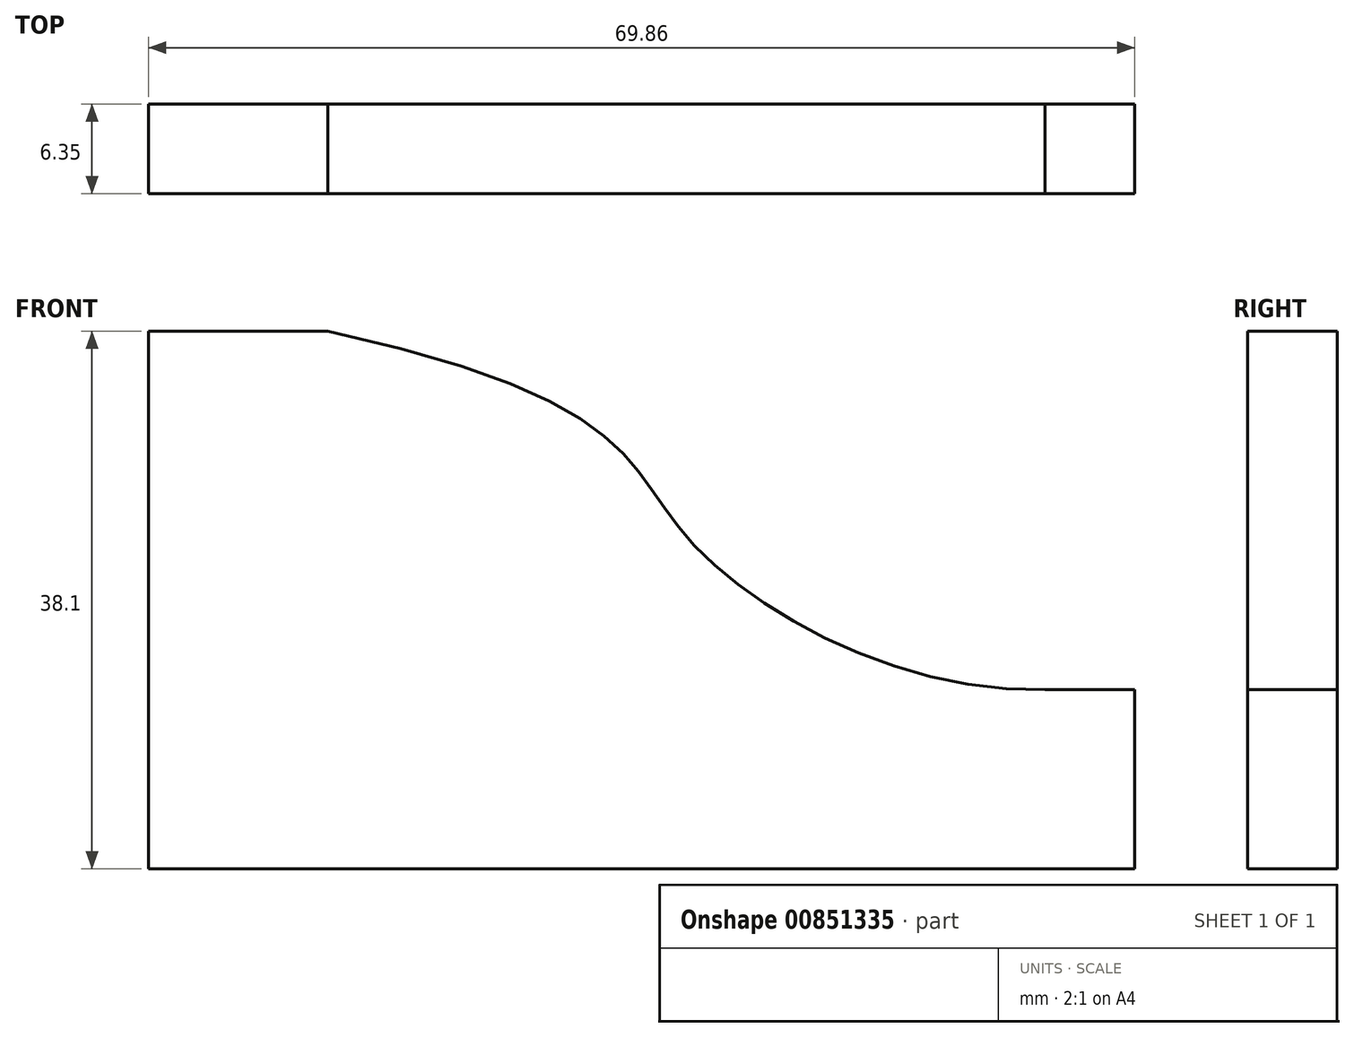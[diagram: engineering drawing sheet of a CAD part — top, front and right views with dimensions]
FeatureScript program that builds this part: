
annotation { "Feature Type Name" : "Feature", "Feature Type Description" : "" }
export const myFeature = defineFeature(function(context is Context, id is Id, definition is map)
    precondition{}
    {
        {
            var Q0;
            Q0=qCreatedBy(makeId("Front.planeOp"),FACE);
            var sketch = newSketch(context, id + "F0", { "sketchPlane" : qUnion([Q0])});
            skLineSegment(sketch, "E0", {"start": v(-34.93, 19.05) * mm, "end": v(-34.93, -19.05) * mm});
            skLineSegment(sketch, "E1", {"start": v(-34.93, -19.05) * mm, "end": v(34.92, -19.05) * mm});
            skLineSegment(sketch, "E2", {"start": v(34.92, -19.05) * mm, "end": v(34.92, -6.35) * mm});
            skLineSegment(sketch, "E3", {"start": v(-34.93, 19.05) * mm, "end": v(-22.23, 19.05) * mm});
            skLineSegment(sketch, "E4", {"start": v(34.92, -6.35) * mm, "end": v(28.58, -6.35) * mm});
            skFitSpline(sketch, "E5", {"points": [v(-22.23, 19.05) * mm, v(3.43, 4.2) * mm, v(28.58, -6.35) * mm], "startDerivative": vector(130.63, -28.71) * mm, "endDerivative": vector(63.2, 1.78) * mm});
            skSolve(sketch);
        }
        {
            var Q0;
            Q0 = qSketchRegion(id + "F0", true);
            extrude(context, id + "F1", {"entities" : qUnion([Q0]), "depth" : 6.35 * mm, "offsetDistance" : 25.4 * mm});
        }
    });
